# Revit family: PRD_FrankeWS_SpprtRls_GrabRail_CNTX700WA
name_source: partatom
category: Furniture
revit_build: Autodesk Revit 2018 (Build: 20190510_1515(x64)
units: mm (PartAtom-declared; Revit-internal decimal feet)

## family parameters
Cut with Voids When Loaded = No
Host = Face
OmniClass Number = 23.40.20.21
OmniClass Title = Toilet and Bath Specialties
Room Calculation Point = No
Shared = No

## types (1)
- CNTX700WA
    AssetType = Fixed
    BIMObjectName = PRD_AR_SpprtRls_GrabRail_CNTX700WA
    Category = Pr_40_20_76_84, Support rails
    Color = Stainless steel
    Default Elevation = 680 mm  [stored 2.23097 ft]
    Description = Angle Grab Rail, 135° angle grab rail for wall mounting, stainless steel, surface satin finished, rough polishing for better surface feel,
32 mm pipe diameter, material thickness 1.2 mm, wall distance 82 mm, with two stainless steel covers for hidden mounting, inclusive
stainless steel screws and dowels.
    DurationUnit = year
    Features = stainless steel, 1.20 mm, satin finished, wall mounting
    Finish = Satin finished
    GrabRailMaterial = PRD_AR_StainlessSteel_SatinFinished
    GrossWeight = 1.32 kg
    IfcExportAs = IfcFurnitureType
    IfcExportType = NOTDEFINED
    MainColor = Stainless steel
    Manufacturer = KWC Group AG
    ManufacturerName = KWC Group AG
    ManufacturerURL = www.kwc.com
    Material = Stainless steel
    MaterialFinish = Satin finished
    MaterialThickness = 1.2 mm  [stored 0.00393701 ft]
    MaterialsBody = Stainless steel 1.4301
    Model = CNTX700WA
    ModelNumber = 2030037502
    ModelReference = CNTX700WA
    NBSDescription = Support rails
    NBSReference = 45-35-72/360
    Name = Grab Rail CNTX700WA
    NetWeight = 0.99 kg
    NominalDepth = 82 mm  [stored 0.269029 ft]
    NominalHeight = 334 mm  [stored 1.0958 ft]
    NominalWidth = 696 mm  [stored 2.28346 ft]
    OverallDepth = 82 mm  [stored 0.269029 ft]
    OverallHeight = 334 mm  [stored 1.0958 ft]
    OverallWidth = 696 mm  [stored 2.28346 ft]
    PipeDiameter = 32 mm  [stored 0.104987 ft]
    ProductInformation = https://pim.kwc.com
    Size = 696x334x82mm
    TypeOfMounting = Wall mounting
    URL = www.kwc.com
    Uniclass2015Code = Pr_40_20_76_84
    Uniclass2015Title = Support rails
    Uniclass2015Version = Products v1.10
    Version = 1
    WarrantyDurationUnit = year

note: [stored X ft] marks values corroborated as IEEE doubles in the binary element streams (Revit-internal decimal feet)

## geometry (parser evidence)
native form markers: Sweep x2
no freeform markers — native parametric forms only
